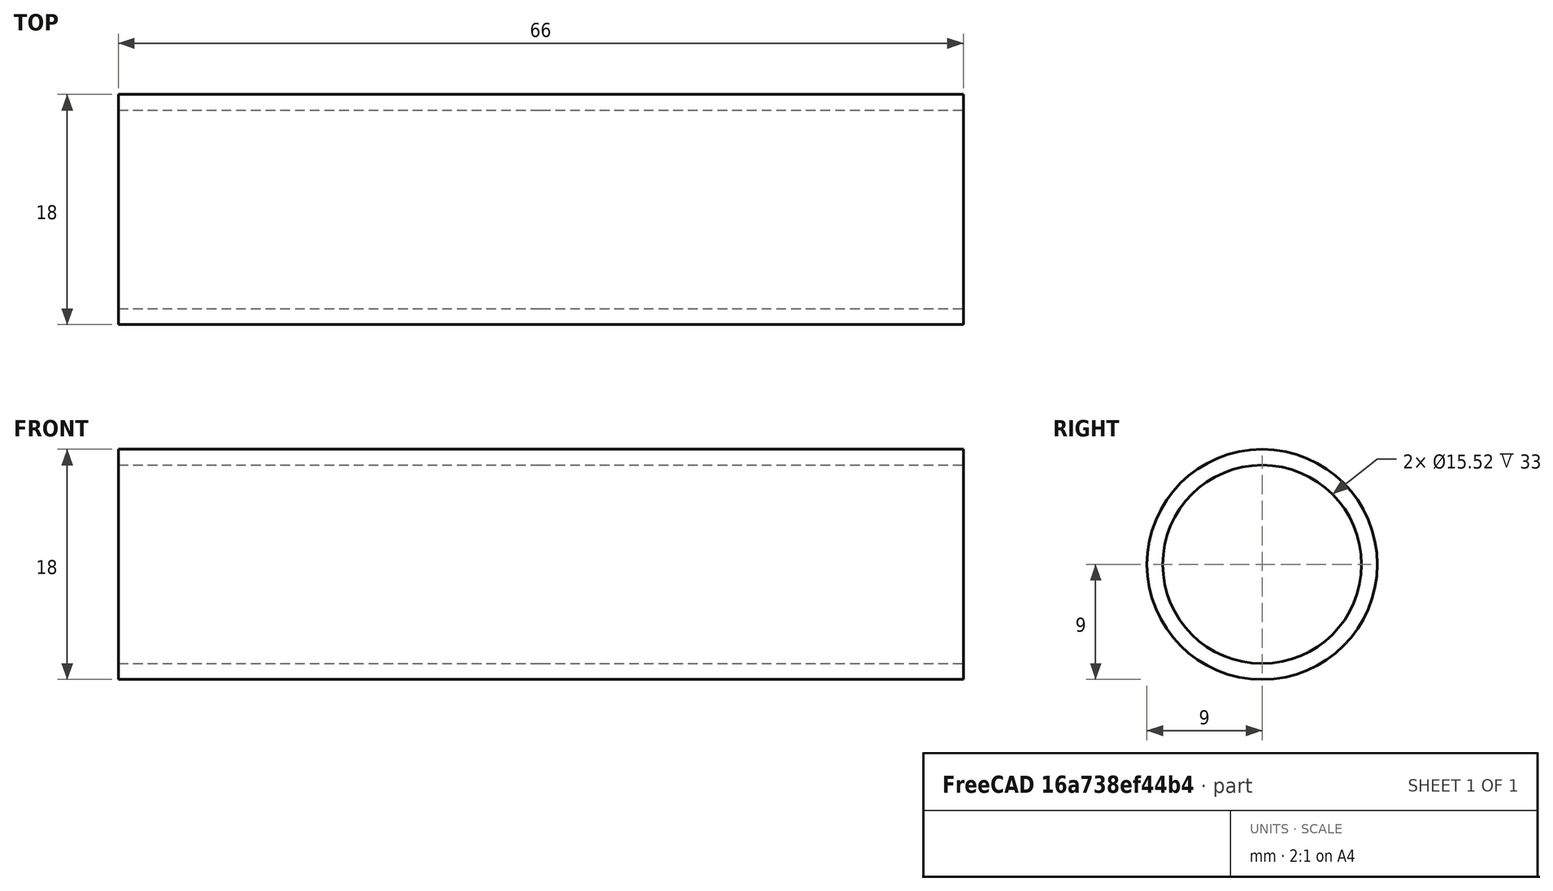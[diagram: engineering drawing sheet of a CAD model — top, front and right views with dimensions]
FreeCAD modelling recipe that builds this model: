
FCSTD DOCUMENT  (FreeCAD 0.21R33771 (Git))
Label: BATTERY
License: All rights reserved
LicenseURL: http://en.wikipedia.org/wiki/All_rights_reserved
objects: Sketcher::SketchObject×1, PartDesign::Revolution×1, PartDesign::Body×1
note: 4 computed .brp shape members not serialized (recipe doc carries the construction recipe); baked Part::Feature solids carry a one-line shape summary decoded from their .brp

FEATURE [Sketcher::SketchObject] Sketch
  FullyConstrained = false
  MapMode = 5
  Support = -> [XY_Plane]
  sketch-geometry (5):
    g0: LineSegment StartX=-33 StartY=7.76224 StartZ=0 EndX=-33 EndY=9 EndZ=0
    g1: LineSegment StartX=-33 StartY=9 StartZ=0 EndX=33 EndY=9 EndZ=0
    g2: LineSegment StartX=33 StartY=9 StartZ=0 EndX=33 EndY=7.76224 EndZ=0
    g3: LineSegment StartX=-33 StartY=7.76224 StartZ=0 EndX=0 EndY=7.76224 EndZ=0
    g4: LineSegment StartX=0 StartY=7.76224 StartZ=0 EndX=33 EndY=7.76224 EndZ=0
  constraints (14):
    c: Coincident(g0,g1)
    c: Coincident(g1,g2)
    c: Horizontal(g1)
    c: Vertical(g0)
    c: Vertical(g2)
    c: DistanceX(g1,g1) = 66
    c: Coincident(g3,g0)
    c: PointOnObject(g3,g-2)
    c: Horizontal(g3)
    c: Coincident(g4,g3)
    c: Coincident(g4,g2)
    c: Horizontal(g4)
    c: Equal(g4,g3)
    c: DistanceY(g-1,g1) = 9
FEATURE [PartDesign::Revolution] Revolution
  Angle = 360
  Axis = (1,0,0)
  Base = (0,0,0)
  Profile = -> Sketch
  ReferenceAxis = -> X_Axis
FEATURE [PartDesign::Body] Body
  Group = -> [Sketch,Revolution]
  Origin = -> Origin
  Tip = -> Revolution
